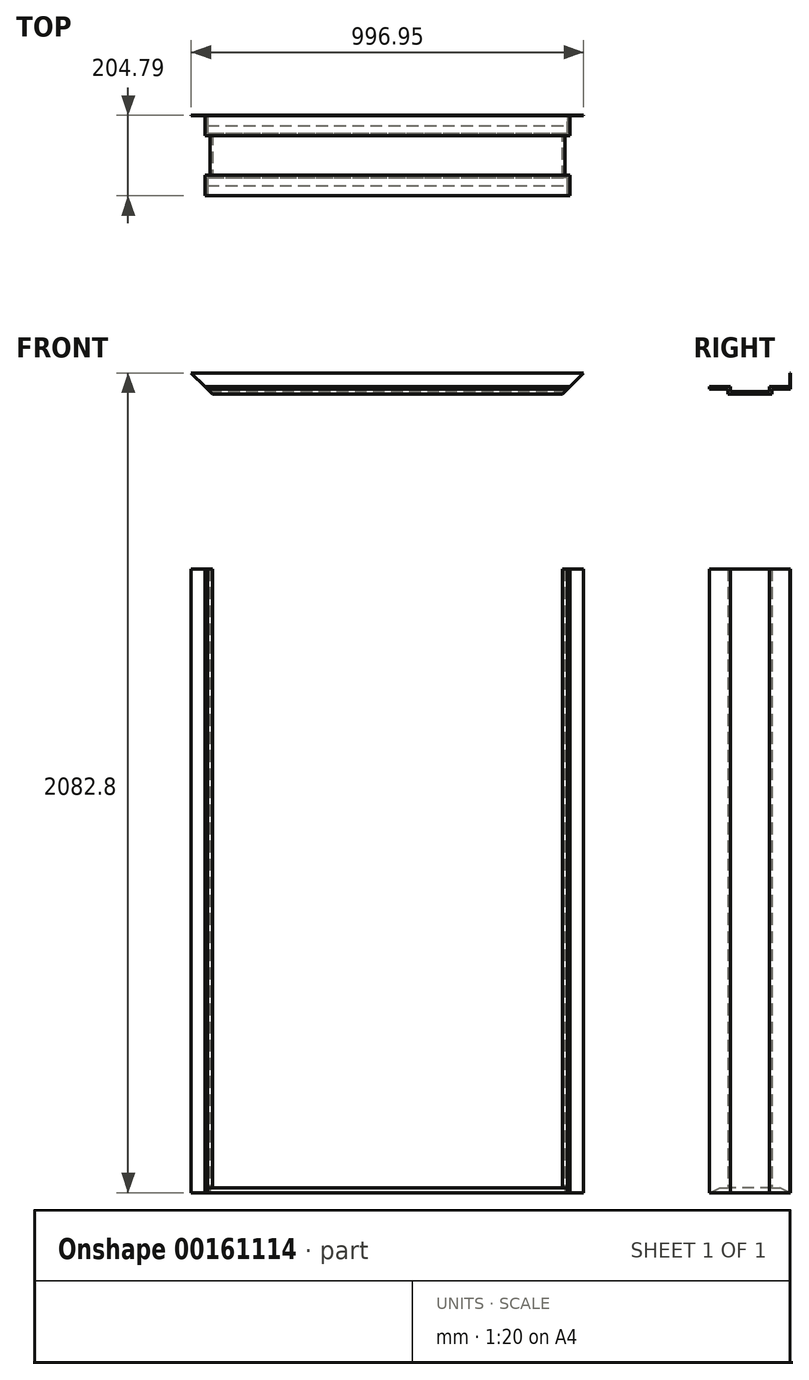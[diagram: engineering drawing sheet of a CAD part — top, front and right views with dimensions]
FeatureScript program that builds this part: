
annotation { "Feature Type Name" : "Feature", "Feature Type Description" : "" }
export const myFeature = defineFeature(function(context is Context, id is Id, definition is map)
    precondition{}
    {
        {
            var Q0;
            Q0=qCreatedBy(makeId("Top.planeOp"),FACE);
            var sketch = newSketch(context, id + "F0", { "sketchPlane" : qUnion([Q0])});
            skLineSegment(sketch, "E0", {"start": v(-41.28, 0) * mm, "end": v(0, 0) * mm});
            skLineSegment(sketch, "E1", {"start": v(-498.48, 0) * mm, "end": v(-498.48, 102.45) * mm, "construction": true});
            skLineSegment(sketch, "E2", {"start": v(0, 0) * mm, "end": v(0, 0.8) * mm});
            skLineSegment(sketch, "E3", {"start": v(0, 0.8) * mm, "end": v(-34.93, 0.8) * mm});
            skLineSegment(sketch, "E4", {"start": v(-34.93, 204) * mm, "end": v(0, 204) * mm});
            skLineSegment(sketch, "E5", {"start": v(0, 204) * mm, "end": v(0, 204.79) * mm});
            skLineSegment(sketch, "E6", {"start": v(0, 204.79) * mm, "end": v(-41.28, 204.79) * mm});
            skLineSegment(sketch, "E7.bottom", {"start": v(-41.28, 46.04) * mm, "end": v(-53.97, 46.04) * mm});
            skLineSegment(sketch, "E7.top", {"start": v(-41.28, 158.75) * mm, "end": v(-53.98, 158.75) * mm});
            skLineSegment(sketch, "E7.right", {"start": v(-53.98, 46.04) * mm, "end": v(-53.98, 158.75) * mm});
            skLineSegment(sketch, "E8", {"start": v(-41.28, 204.79) * mm, "end": v(-41.28, 158.75) * mm});
            skLineSegment(sketch, "E9", {"start": v(-41.28, 46.04) * mm, "end": v(-41.28, 0) * mm});
            skLineSegment(sketch, "E10", {"start": v(-34.93, 204) * mm, "end": v(-34.93, 152.4) * mm});
            skLineSegment(sketch, "E11", {"start": v(-47.62, 152.4) * mm, "end": v(-47.62, 52.39) * mm});
            skLineSegment(sketch, "E12", {"start": v(-47.62, 52.39) * mm, "end": v(-34.93, 52.39) * mm});
            skLineSegment(sketch, "E13", {"start": v(-34.93, 52.39) * mm, "end": v(-34.93, 0.8) * mm});
            skLineSegment(sketch, "E14", {"start": v(-47.62, 152.4) * mm, "end": v(-34.93, 152.4) * mm});
            skLineSegment(sketch, "E15.MirrorCS", {"start": v(-996.95, 0) * mm, "end": v(-996.95, 0.8) * mm});
            skLineSegment(sketch, "E16.MirrorCS", {"start": v(-996.95, 204) * mm, "end": v(-996.95, 204.79) * mm});
            skLineSegment(sketch, "E17.MirrorCS", {"start": v(-949.33, 52.39) * mm, "end": v(-962.03, 52.39) * mm});
            skLineSegment(sketch, "E18.MirrorCS", {"start": v(-949.33, 152.4) * mm, "end": v(-962.02, 152.4) * mm});
            skLineSegment(sketch, "E19.MirrorCS", {"start": v(-955.68, 46.04) * mm, "end": v(-942.98, 46.04) * mm});
            skLineSegment(sketch, "E20.MirrorCS", {"start": v(-955.68, 158.75) * mm, "end": v(-942.98, 158.75) * mm});
            skLineSegment(sketch, "E21.MirrorCS", {"start": v(-962.02, 204) * mm, "end": v(-996.95, 204) * mm});
            skLineSegment(sketch, "E22.MirrorCS", {"start": v(-955.68, 0) * mm, "end": v(-996.95, 0) * mm});
            skLineSegment(sketch, "E23.MirrorCS", {"start": v(-962.03, 204) * mm, "end": v(-962.03, 152.4) * mm});
            skLineSegment(sketch, "E24.MirrorCS", {"start": v(-955.68, 46.04) * mm, "end": v(-955.68, 0) * mm});
            skLineSegment(sketch, "E25.MirrorCS", {"start": v(-942.98, 46.04) * mm, "end": v(-942.98, 158.75) * mm});
            skLineSegment(sketch, "E26.MirrorCS", {"start": v(-955.68, 204.79) * mm, "end": v(-955.68, 158.75) * mm});
            skLineSegment(sketch, "E27.MirrorCS", {"start": v(-996.95, 204.79) * mm, "end": v(-955.68, 204.79) * mm});
            skLineSegment(sketch, "E28.MirrorCS", {"start": v(-949.33, 152.4) * mm, "end": v(-949.33, 52.39) * mm});
            skLineSegment(sketch, "E29.MirrorCS", {"start": v(-962.03, 52.39) * mm, "end": v(-962.03, 0.8) * mm});
            skLineSegment(sketch, "E30.MirrorCS", {"start": v(-996.95, 0.8) * mm, "end": v(-962.03, 0.8) * mm});
            skSolve(sketch);
        }
        {
            var Q0;
            Q0=qSketchRegion(id+"F0",true);
            extrude(context, id + "F1", {"entities" : qUnion([Q0]), "depth" : 2082.8 * mm});
        }
        {
            var Q0;
            Q0=qCreatedBy(makeId("Front.planeOp"),FACE);
            var sketch = newSketch(context, id + "F2", { "sketchPlane" : qUnion([Q0])});
            skPoint(sketch, "E31.0", {"position": v(-996.95, 2082.8) * mm});
            skPoint(sketch, "E32.0", {"position": v(0, 2082.8) * mm});
            skLineSegment(sketch, "E33", {"start": v(-996.95, 2082.8) * mm, "end": v(-498.48, 1584.33) * mm});
            skLineSegment(sketch, "E34", {"start": v(-498.48, 1584.33) * mm, "end": v(0, 2082.8) * mm});
            skLineSegment(sketch, "E35", {"start": v(-996.95, 2082.8) * mm, "end": v(0, 2082.8) * mm});
            skSolve(sketch);
        }
        {
            var Q0;
            Q0=qSketchRegion(id+"F2",true);
            extrude(context, id + "F3", {"entities" : qUnion([Q0]), "operationType" : NewBodyOperationType.REMOVE, "endBound" : BoundingType.THROUGH_ALL, "oppositeDirection" : true, "depth" : 25.4 * mm});
        }
        {
            var Q0;
            Q0=qCreatedBy(makeId("Right.planeOp"),FACE);
            var sketch = newSketch(context, id + "F4", { "sketchPlane" : qUnion([Q0])});
            skLineSegment(sketch, "E36.0.0", {"start": v(204.79, 2041.53) * mm, "end": v(158.75, 2041.53) * mm});
            skLineSegment(sketch, "E36.0.1", {"start": v(158.75, 2041.53) * mm, "end": v(158.75, 2028.83) * mm});
            skLineSegment(sketch, "E36.0.2", {"start": v(158.75, 2028.83) * mm, "end": v(46.04, 2028.83) * mm});
            skLineSegment(sketch, "E36.0.3", {"start": v(46.04, 2028.83) * mm, "end": v(46.04, 2041.53) * mm});
            skLineSegment(sketch, "E36.0.4", {"start": v(46.04, 2041.53) * mm, "end": v(0, 2041.53) * mm});
            skLineSegment(sketch, "E36.0.5", {"start": v(0, 2041.53) * mm, "end": v(0, 2082.8) * mm});
            skLineSegment(sketch, "E36.0.6", {"start": v(0, 2082.8) * mm, "end": v(0.8, 2082.8) * mm});
            skLineSegment(sketch, "E36.0.7", {"start": v(0.8, 2082.8) * mm, "end": v(0.8, 2047.88) * mm});
            skLineSegment(sketch, "E36.0.8", {"start": v(0.8, 2047.88) * mm, "end": v(52.39, 2047.88) * mm});
            skLineSegment(sketch, "E36.0.9", {"start": v(52.39, 2047.88) * mm, "end": v(52.39, 2035.18) * mm});
            skLineSegment(sketch, "E36.0.10", {"start": v(52.39, 2035.18) * mm, "end": v(152.4, 2035.18) * mm});
            skLineSegment(sketch, "E36.0.11", {"start": v(152.4, 2035.18) * mm, "end": v(152.4, 2047.88) * mm});
            skLineSegment(sketch, "E36.0.12", {"start": v(152.4, 2047.88) * mm, "end": v(204, 2047.88) * mm});
            skLineSegment(sketch, "E36.0.13", {"start": v(204, 2047.88) * mm, "end": v(204, 2082.8) * mm});
            skLineSegment(sketch, "E36.0.14", {"start": v(204, 2082.8) * mm, "end": v(204.79, 2082.8) * mm});
            skLineSegment(sketch, "E36.0.15", {"start": v(204.79, 2082.8) * mm, "end": v(204.79, 2041.53) * mm});
            skSolve(sketch);
        }
        {
            var Q0;
            Q0=qSketchRegion(id+"F4",true);
            var Q1;
            Q1=makeQuery(id+"F1.opExtrude","SWEPT_FACE",FACE,{"disambiguationData":[OSD([sQuery(id+"F0.wireOp",EDGE,"E15.MirrorCS")])]});
            extrude(context, id + "F5", {"entities" : qUnion([Q0]), "endBound" : BoundingType.UP_TO_SURFACE, "oppositeDirection" : true, "endBoundEntityFace" : qUnion([Q1]), "depth" : 914.4 * mm});
        }
        {
            var Q0;
            Q0=qCreatedBy(makeId("Front.planeOp"),FACE);
            var sketch = newSketch(context, id + "F6", { "sketchPlane" : qUnion([Q0])});
            skLineSegment(sketch, "E37.0", {"start": v(-996.95, 2082.8) * mm, "end": v(-498.48, 1584.33) * mm});
            skLineSegment(sketch, "E38.0", {"start": v(-498.48, 1584.33) * mm, "end": v(0, 2082.8) * mm});
            skLineSegment(sketch, "E39", {"start": v(-996.95, 2082.8) * mm, "end": v(-1301.75, 2082.8) * mm});
            skLineSegment(sketch, "E40", {"start": v(-1301.75, 2082.8) * mm, "end": v(-1301.75, 1584.33) * mm});
            skLineSegment(sketch, "E41", {"start": v(-1301.75, 1584.33) * mm, "end": v(-498.48, 1584.33) * mm});
            skLineSegment(sketch, "E42", {"start": v(-498.48, 1584.33) * mm, "end": v(-498.48, 1830.19) * mm, "construction": true});
            skLineSegment(sketch, "E43.MirrorCS", {"start": v(0, 2082.8) * mm, "end": v(304.8, 2082.8) * mm});
            skLineSegment(sketch, "E44.MirrorCS", {"start": v(304.8, 2082.8) * mm, "end": v(304.8, 1584.33) * mm});
            skLineSegment(sketch, "E45.MirrorCS", {"start": v(304.8, 1584.33) * mm, "end": v(-498.48, 1584.33) * mm});
            skSolve(sketch);
        }
        {
            var Q0;
            Q0 = qSketchRegion(id + "F6", true);
            extrude(context, id + "F7", {"entities" : qUnion([Q0]), "operationType" : NewBodyOperationType.REMOVE, "endBound" : BoundingType.THROUGH_ALL, "oppositeDirection" : true, "depth" : 25.4 * mm});
        }
        {
            var Q0;
            Q0=makeQuery(id+"F1.opExtrude","SWEPT_BODY",BODY,{"disambiguationData":[OSD([sQuery(id+"F0.wireOp",EDGE,"E0"),sQuery(id+"F0.wireOp",EDGE,"E2"),sQuery(id+"F0.wireOp",EDGE,"E3"),sQuery(id+"F0.wireOp",EDGE,"E4"),sQuery(id+"F0.wireOp",EDGE,"E5"),sQuery(id+"F0.wireOp",EDGE,"E6"),sQuery(id+"F0.wireOp",EDGE,"E7.bottom"),sQuery(id+"F0.wireOp",EDGE,"E7.top"),sQuery(id+"F0.wireOp",EDGE,"E7.right"),sQuery(id+"F0.wireOp",EDGE,"E8"),sQuery(id+"F0.wireOp",EDGE,"E9"),sQuery(id+"F0.wireOp",EDGE,"E10"),sQuery(id+"F0.wireOp",EDGE,"E11"),sQuery(id+"F0.wireOp",EDGE,"E12"),sQuery(id+"F0.wireOp",EDGE,"E13"),sQuery(id+"F0.wireOp",EDGE,"E14")])]});
            var Q1;
            Q1=makeQuery(id+"F1.opExtrude","SWEPT_BODY",BODY,{"disambiguationData":[OSD([sQuery(id+"F0.wireOp",EDGE,"E15.MirrorCS"),sQuery(id+"F0.wireOp",EDGE,"E16.MirrorCS"),sQuery(id+"F0.wireOp",EDGE,"E17.MirrorCS"),sQuery(id+"F0.wireOp",EDGE,"E18.MirrorCS"),sQuery(id+"F0.wireOp",EDGE,"E19.MirrorCS"),sQuery(id+"F0.wireOp",EDGE,"E20.MirrorCS"),sQuery(id+"F0.wireOp",EDGE,"E21.MirrorCS"),sQuery(id+"F0.wireOp",EDGE,"E22.MirrorCS"),sQuery(id+"F0.wireOp",EDGE,"E23.MirrorCS"),sQuery(id+"F0.wireOp",EDGE,"E24.MirrorCS"),sQuery(id+"F0.wireOp",EDGE,"E25.MirrorCS"),sQuery(id+"F0.wireOp",EDGE,"E26.MirrorCS"),sQuery(id+"F0.wireOp",EDGE,"E27.MirrorCS"),sQuery(id+"F0.wireOp",EDGE,"E28.MirrorCS"),sQuery(id+"F0.wireOp",EDGE,"E29.MirrorCS"),sQuery(id+"F0.wireOp",EDGE,"E30.MirrorCS")])]});
            var Q2;
            Q2=makeQuery(id+"F5.opExtrude","SWEPT_BODY",BODY,{"disambiguationData":[OSD([sQuery(id+"F4.wireOp",EDGE,"E36.0.0"),sQuery(id+"F4.wireOp",EDGE,"E36.0.1"),sQuery(id+"F4.wireOp",EDGE,"E36.0.2"),sQuery(id+"F4.wireOp",EDGE,"E36.0.3"),sQuery(id+"F4.wireOp",EDGE,"E36.0.4"),sQuery(id+"F4.wireOp",EDGE,"E36.0.5"),sQuery(id+"F4.wireOp",EDGE,"E36.0.6"),sQuery(id+"F4.wireOp",EDGE,"E36.0.7"),sQuery(id+"F4.wireOp",EDGE,"E36.0.8"),sQuery(id+"F4.wireOp",EDGE,"E36.0.9"),sQuery(id+"F4.wireOp",EDGE,"E36.0.10"),sQuery(id+"F4.wireOp",EDGE,"E36.0.11"),sQuery(id+"F4.wireOp",EDGE,"E36.0.12"),sQuery(id+"F4.wireOp",EDGE,"E36.0.13"),sQuery(id+"F4.wireOp",EDGE,"E36.0.14"),sQuery(id+"F4.wireOp",EDGE,"E36.0.15")])]});
            booleanBodies(context, id + "F8", {"operationType" : BooleanOperationType.UNION, "tools" : qUnion([Q0, Q1, Q2])});
        }
        {
            var Q0;
            Q0=makeQuery(id+"F1.opExtrude","SWEPT_FACE",FACE,{"disambiguationData":[OSD([sQuery(id+"F0.wireOp",EDGE,"E9")])]});
            var sketch = newSketch(context, id + "F9", { "sketchPlane" : qUnion([Q0])});
            skPoint(sketch, "E46.0", {"position": v(-102.4, 0) * mm});
            skLineSegment(sketch, "E47", {"start": v(-102.4, 0) * mm, "end": v(-204, 0) * mm});
            skLineSegment(sketch, "E48", {"start": v(-204, 0) * mm, "end": v(-178.6, 12.7) * mm});
            skLineSegment(sketch, "E49", {"start": v(-178.6, 12.7) * mm, "end": v(-102.4, 12.7) * mm});
            skLineSegment(sketch, "E50", {"start": v(-102.4, 0) * mm, "end": v(-102.4, 12.7) * mm, "construction": true});
            skLineSegment(sketch, "E51.MirrorCS", {"start": v(-102.4, 0) * mm, "end": v(-0.8, 0) * mm});
            skLineSegment(sketch, "E52.MirrorCS", {"start": v(-26.2, 12.7) * mm, "end": v(-102.4, 12.7) * mm});
            skLineSegment(sketch, "E53.MirrorCS", {"start": v(-0.8, 0) * mm, "end": v(-26.2, 12.7) * mm});
            skSolve(sketch);
        }
        {
            var Q0;
            Q0 = qSketchRegion(id + "F9", true);
            var Q1;
            Q1=makeQuery(id+"F1.opExtrude","SWEPT_FACE",FACE,{"disambiguationData":[OSD([sQuery(id+"F0.wireOp",EDGE,"E24.MirrorCS")])]});
            extrude(context, id + "F10", {"entities" : qUnion([Q0]), "operationType" : NewBodyOperationType.ADD, "endBound" : BoundingType.UP_TO_SURFACE, "endBoundEntityFace" : qUnion([Q1]), "depth" : 25.4 * mm});
        }
        {
            var Q0;
            Q0=makeQuery(id+"F8.opBoolean","MERGE",FACE,{"derivedFrom":[makeQuery(id+"F1.opExtrude","SWEPT_FACE",FACE,{"disambiguationData":[OSD([sQuery(id+"F0.wireOp",EDGE,"E3")])]}),makeQuery(id+"F1.opExtrude","SWEPT_FACE",FACE,{"disambiguationData":[OSD([sQuery(id+"F0.wireOp",EDGE,"E30.MirrorCS")])]}),makeQuery(id+"F5.opExtrude","SWEPT_FACE",FACE,{"disambiguationData":[OSD([sQuery(id+"F4.wireOp",EDGE,"E36.0.7")])]})]});
            var sketch = newSketch(context, id + "F11", { "sketchPlane" : qUnion([Q0])});
            skLineSegment(sketch, "E54.0", {"start": v(962.02, 2047.88) * mm, "end": v(962.02, 0) * mm});
            skLineSegment(sketch, "E55.0", {"start": v(962.02, 0) * mm, "end": v(996.95, 0) * mm});
            skLineSegment(sketch, "E56.0", {"start": v(996.95, 2082.8) * mm, "end": v(996.95, 0) * mm});
            skLineSegment(sketch, "E57.0", {"start": v(996.95, 2082.8) * mm, "end": v(0, 2082.8) * mm});
            skLineSegment(sketch, "E58.0", {"start": v(0, 2082.8) * mm, "end": v(0, 0) * mm});
            skLineSegment(sketch, "E59.0", {"start": v(962.03, 2047.88) * mm, "end": v(34.93, 2047.88) * mm});
            skLineSegment(sketch, "E60.0", {"start": v(34.93, 2047.88) * mm, "end": v(34.93, 0) * mm});
            skLineSegment(sketch, "E61.0", {"start": v(34.93, 0) * mm, "end": v(0, 0) * mm});
            skSolve(sketch);
        }
        {
            var Q0;
            Q0 = qSketchRegion(id + "F11", true);
            extrude(context, id + "F12", {"entities" : qUnion([Q0]), "operationType" : NewBodyOperationType.REMOVE, "endBound" : BoundingType.THROUGH_ALL, "oppositeDirection" : true, "depth" : 728.98 * mm});
        }
        {
            var Q0;
            Q0=qCreatedBy(makeId("Top.planeOp"),FACE);
            var sketch = newSketch(context, id + "F13", { "sketchPlane" : qUnion([Q0])});
            skLineSegment(sketch, "E62.0.0", {"start": v(-47.62, 52.39) * mm, "end": v(-41.28, 52.39) * mm});
            skLineSegment(sketch, "E62.0.1", {"start": v(-41.28, 52.39) * mm, "end": v(-41.28, 152.4) * mm});
            skLineSegment(sketch, "E62.0.2", {"start": v(-41.28, 152.4) * mm, "end": v(-47.62, 152.4) * mm});
            skLineSegment(sketch, "E62.0.3", {"start": v(-47.62, 152.4) * mm, "end": v(-47.62, 52.39) * mm});
            skLineSegment(sketch, "E63.0.0", {"start": v(-955.67, 52.39) * mm, "end": v(-949.33, 52.39) * mm});
            skLineSegment(sketch, "E63.0.1", {"start": v(-949.33, 52.39) * mm, "end": v(-949.33, 152.4) * mm});
            skLineSegment(sketch, "E63.0.2", {"start": v(-949.33, 152.4) * mm, "end": v(-955.67, 152.4) * mm});
            skLineSegment(sketch, "E63.0.3", {"start": v(-955.67, 152.4) * mm, "end": v(-955.67, 52.39) * mm});
            skSolve(sketch);
        }
        {
            var Q0;
            Q0 = qSketchRegion(id + "F13", true);
            extrude(context, id + "F14", {"entities" : qUnion([Q0]), "operationType" : NewBodyOperationType.REMOVE, "endBound" : BoundingType.THROUGH_ALL, "depth" : 25.4 * mm});
        }
    });
